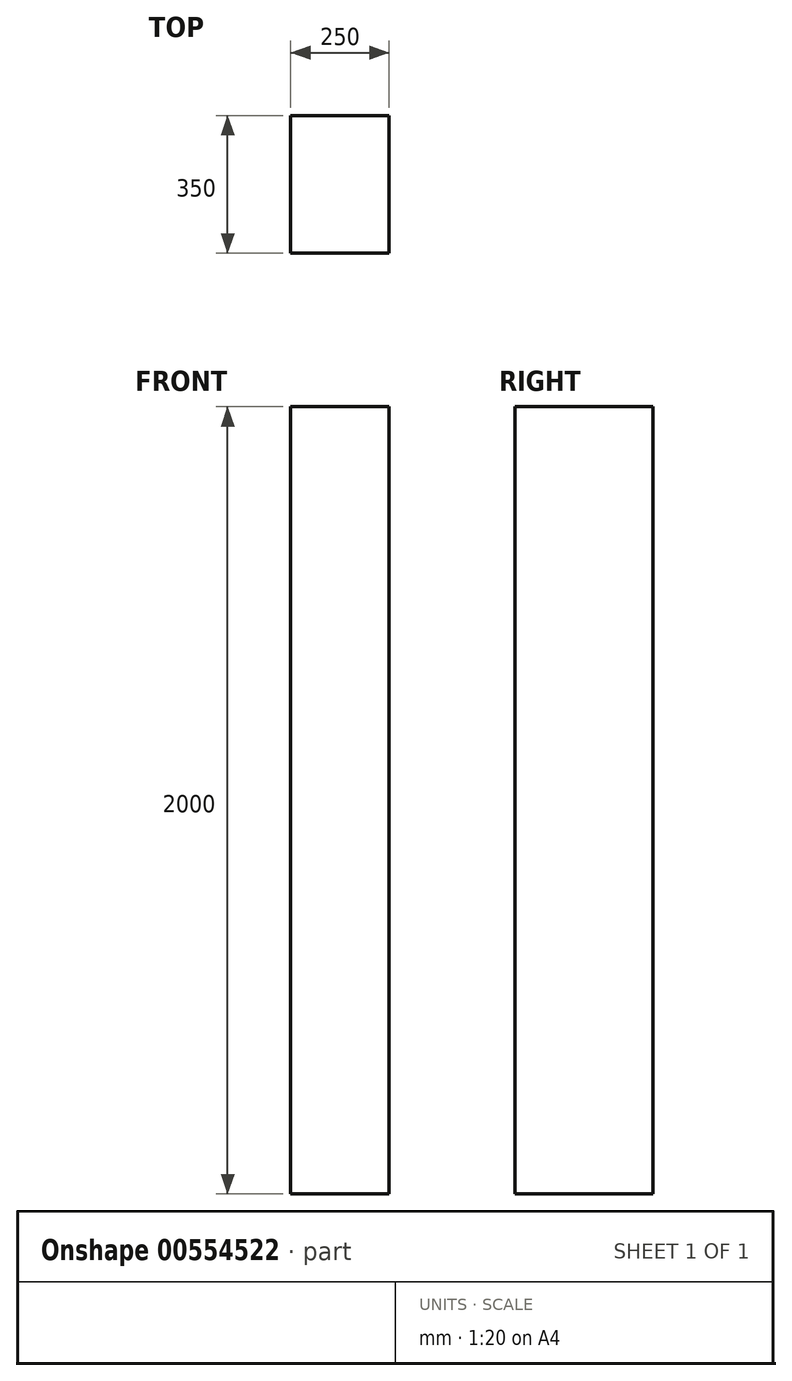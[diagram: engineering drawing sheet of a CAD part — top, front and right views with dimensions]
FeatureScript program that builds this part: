
annotation { "Feature Type Name" : "Feature", "Feature Type Description" : "" }
export const myFeature = defineFeature(function(context is Context, id is Id, definition is map)
    precondition{}
    {
        {
            var Q0;
            Q0=qCreatedBy(makeId("Top.planeOp"),FACE);
            var sketch = newSketch(context, id + "F0", { "sketchPlane" : qUnion([Q0])});
            skLineSegment(sketch, "E0.bottom", {"start": v(125, -175) * mm, "end": v(-125, -175) * mm});
            skLineSegment(sketch, "E0.top", {"start": v(125, 175) * mm, "end": v(-125, 175) * mm});
            skLineSegment(sketch, "E0.left", {"start": v(125, -175) * mm, "end": v(125, 175) * mm});
            skLineSegment(sketch, "E0.right", {"start": v(-125, -175) * mm, "end": v(-125, 175) * mm});
            skPoint(sketch, "E0.middle", {"position": v(0, 0) * mm});
            skSolve(sketch);
        }
        {
            var Q0;
            Q0=makeQuery(id+"F0.imprint","IMPRINT",FACE,{"disambiguationData":[TD([[makeQuery(id+"F0.imprint","IMPRINT",EDGE,{"derivedFrom":sQuery(id+"F0.wireOp",EDGE,"E0.bottom")}),-1.0]])]});
            extrude(context, id + "F1", {"entities" : qUnion([Q0]), "depth" : 2000 * mm, "offsetDistance" : 25 * mm});
        }
    });
